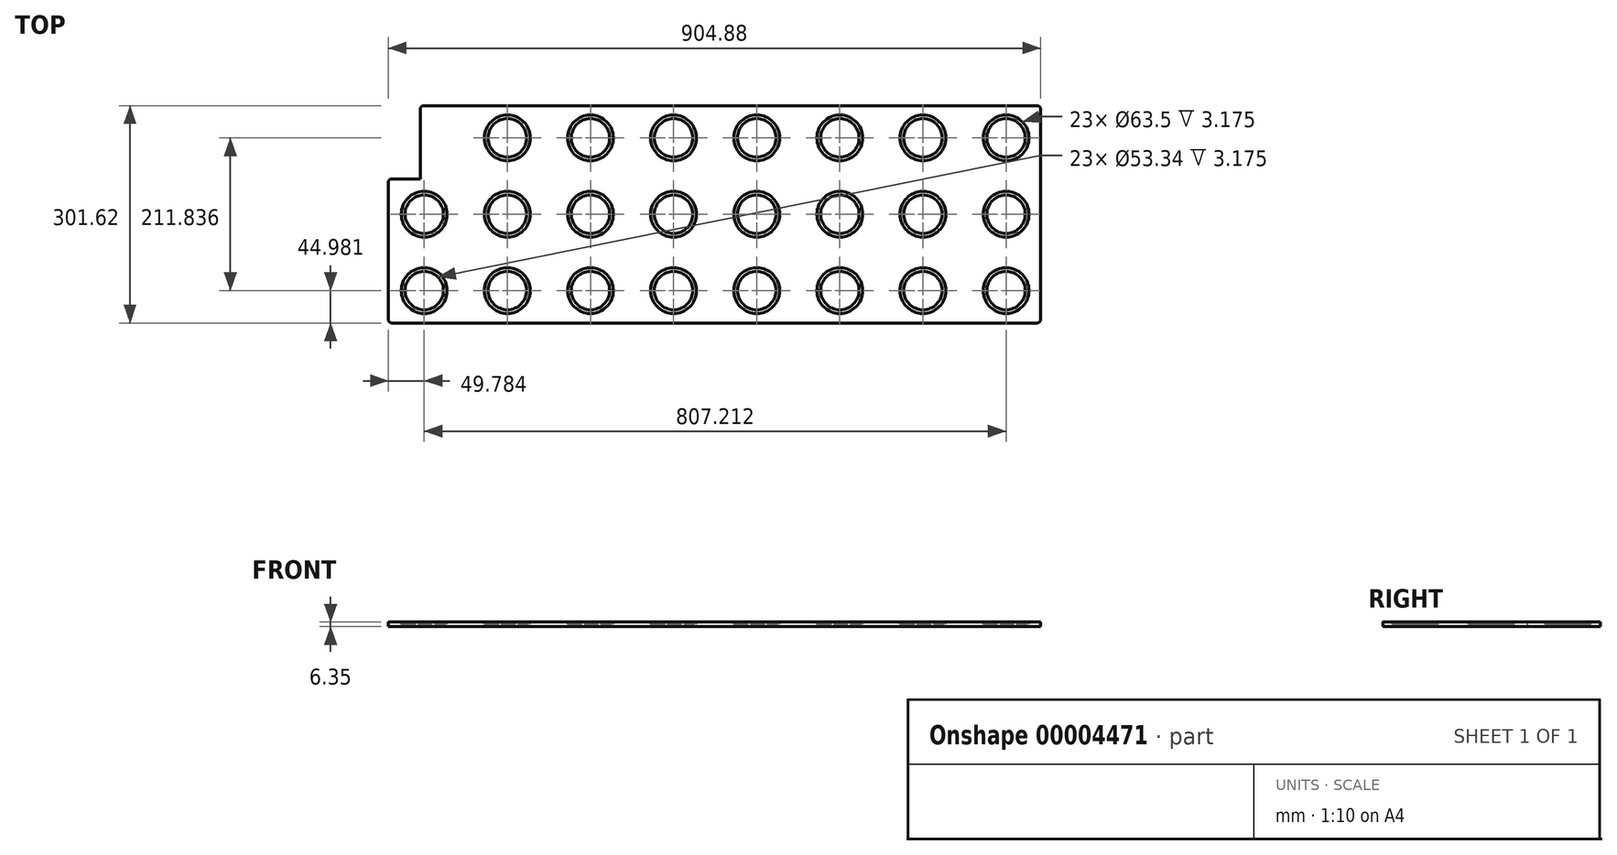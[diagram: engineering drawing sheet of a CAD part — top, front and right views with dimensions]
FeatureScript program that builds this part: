
annotation { "Feature Type Name" : "Feature", "Feature Type Description" : "" }
export const myFeature = defineFeature(function(context is Context, id is Id, definition is map)
    precondition{}
    {
        {
            var Q0;
            Q0=qCreatedBy(makeId("Top.planeOp"),FACE);
            var sketch = newSketch(context, id + "F0", { "sketchPlane" : qUnion([Q0])});
            skLineSegment(sketch, "E0", {"start": v(0, 0) * mm, "end": v(904.88, 0) * mm});
            skLineSegment(sketch, "E1", {"start": v(904.88, 0) * mm, "end": v(904.88, 301.62) * mm});
            skLineSegment(sketch, "E2", {"start": v(904.88, 301.63) * mm, "end": v(44.45, 301.63) * mm});
            skLineSegment(sketch, "E3", {"start": v(44.45, 301.62) * mm, "end": v(44.45, 200.02) * mm});
            skLineSegment(sketch, "E4", {"start": v(44.45, 200.02) * mm, "end": v(0, 200.02) * mm});
            skLineSegment(sketch, "E5", {"start": v(0, 200.02) * mm, "end": v(0, 0) * mm});
            skSolve(sketch);
        }
        {
            var Q0;
            Q0=qSketchRegion(id+"F0",true);
            extrude(context, id + "F1", {"entities" : qUnion([Q0]), "depth" : 6.35 * mm});
        }
        {
            var Q0;
            Q0=makeQuery(id+"F1.opExtrude","CAP_FACE",FACE,{"disambiguationData":[OSD([sQuery(id+"F0.wireOp",EDGE,"E0"),sQuery(id+"F0.wireOp",EDGE,"E1"),sQuery(id+"F0.wireOp",EDGE,"E2"),sQuery(id+"F0.wireOp",EDGE,"E3"),sQuery(id+"F0.wireOp",EDGE,"E4"),sQuery(id+"F0.wireOp",EDGE,"E5")])],"isStart":false});
            var sketch = newSketch(context, id + "F2", { "sketchPlane" : qUnion([Q0])});
            skCircle(sketch, "E6", {"center": v(49.78, 44.98) * mm, "radius": 31.75 * mm});
            skCircle(sketch, "E7.0.1.0", {"center": v(49.78, 150.9) * mm, "radius": 31.75 * mm});
            skCircle(sketch, "E7.1.0.0", {"center": v(165.1, 44.98) * mm, "radius": 31.75 * mm});
            skCircle(sketch, "E7.1.1.0", {"center": v(165.1, 150.9) * mm, "radius": 31.75 * mm});
            skCircle(sketch, "E7.1.2.0", {"center": v(165.1, 256.82) * mm, "radius": 31.75 * mm});
            skCircle(sketch, "E7.2.0.0", {"center": v(280.42, 44.98) * mm, "radius": 31.75 * mm});
            skCircle(sketch, "E7.2.1.0", {"center": v(280.42, 150.9) * mm, "radius": 31.75 * mm});
            skCircle(sketch, "E7.2.2.0", {"center": v(280.42, 256.82) * mm, "radius": 31.75 * mm});
            skCircle(sketch, "E7.3.0.0", {"center": v(395.73, 44.98) * mm, "radius": 31.75 * mm});
            skCircle(sketch, "E7.3.1.0", {"center": v(395.73, 150.9) * mm, "radius": 31.75 * mm});
            skCircle(sketch, "E7.3.2.0", {"center": v(395.73, 256.82) * mm, "radius": 31.75 * mm});
            skCircle(sketch, "E7.4.0.0", {"center": v(511.05, 44.98) * mm, "radius": 31.75 * mm});
            skCircle(sketch, "E7.4.1.0", {"center": v(511.05, 150.9) * mm, "radius": 31.75 * mm});
            skCircle(sketch, "E7.4.2.0", {"center": v(511.05, 256.82) * mm, "radius": 31.75 * mm});
            skCircle(sketch, "E7.5.0.0", {"center": v(626.36, 44.98) * mm, "radius": 31.75 * mm});
            skCircle(sketch, "E7.5.1.0", {"center": v(626.36, 150.9) * mm, "radius": 31.75 * mm});
            skCircle(sketch, "E7.5.2.0", {"center": v(626.36, 256.82) * mm, "radius": 31.75 * mm});
            skCircle(sketch, "E7.6.0.0", {"center": v(741.68, 44.98) * mm, "radius": 31.75 * mm});
            skCircle(sketch, "E7.6.1.0", {"center": v(741.68, 150.9) * mm, "radius": 31.75 * mm});
            skCircle(sketch, "E7.6.2.0", {"center": v(741.68, 256.82) * mm, "radius": 31.75 * mm});
            skCircle(sketch, "E7.7.0.0", {"center": v(857, 44.98) * mm, "radius": 31.75 * mm});
            skCircle(sketch, "E7.7.1.0", {"center": v(857, 150.9) * mm, "radius": 31.75 * mm});
            skCircle(sketch, "E7.7.2.0", {"center": v(857, 256.82) * mm, "radius": 31.75 * mm});
            skLineSegment(sketch, "E7.direction1", {"start": v(49.78, 44.98) * mm, "end": v(165.1, 44.98) * mm, "construction": true});
            skLineSegment(sketch, "E7.direction2", {"start": v(49.78, 44.98) * mm, "end": v(49.78, 150.9) * mm, "construction": true});
            skSolve(sketch);
        }
        {
            var Q0;
            Q0=qSketchRegion(id+"F2",true);
            extrude(context, id + "F3", {"entities" : qUnion([Q0]), "operationType" : NewBodyOperationType.REMOVE, "endBound" : BoundingType.THROUGH_ALL, "oppositeDirection" : true, "depth" : 25.4 * mm});
        }
        {
            var Q0;
            Q0=makeQuery(id+"F1.opExtrude","CAP_FACE",FACE,{"disambiguationData":[OSD([sQuery(id+"F0.wireOp",EDGE,"E0"),sQuery(id+"F0.wireOp",EDGE,"E1"),sQuery(id+"F0.wireOp",EDGE,"E2"),sQuery(id+"F0.wireOp",EDGE,"E3"),sQuery(id+"F0.wireOp",EDGE,"E4"),sQuery(id+"F0.wireOp",EDGE,"E5")])],"isStart":true});
            var sketch = newSketch(context, id + "F4", { "sketchPlane" : qUnion([Q0])});
            skCircle(sketch, "E8", {"center": v(49.78, -44.98) * mm, "radius": 26.67 * mm});
            skCircle(sketch, "E9.0.1.0", {"center": v(49.78, -150.9) * mm, "radius": 26.67 * mm});
            skCircle(sketch, "E9.1.0.0", {"center": v(165.1, -44.98) * mm, "radius": 26.67 * mm});
            skCircle(sketch, "E9.1.1.0", {"center": v(165.1, -150.9) * mm, "radius": 26.67 * mm});
            skCircle(sketch, "E9.1.2.0", {"center": v(165.1, -256.82) * mm, "radius": 26.67 * mm});
            skCircle(sketch, "E9.2.0.0", {"center": v(280.42, -44.98) * mm, "radius": 26.67 * mm});
            skCircle(sketch, "E9.2.1.0", {"center": v(280.42, -150.9) * mm, "radius": 26.67 * mm});
            skCircle(sketch, "E9.2.2.0", {"center": v(280.42, -256.82) * mm, "radius": 26.67 * mm});
            skCircle(sketch, "E9.3.0.0", {"center": v(395.73, -44.98) * mm, "radius": 26.67 * mm});
            skCircle(sketch, "E9.3.1.0", {"center": v(395.73, -150.9) * mm, "radius": 26.67 * mm});
            skCircle(sketch, "E9.3.2.0", {"center": v(395.73, -256.82) * mm, "radius": 26.67 * mm});
            skCircle(sketch, "E9.4.0.0", {"center": v(511.05, -44.98) * mm, "radius": 26.67 * mm});
            skCircle(sketch, "E9.4.1.0", {"center": v(511.05, -150.9) * mm, "radius": 26.67 * mm});
            skCircle(sketch, "E9.4.2.0", {"center": v(511.05, -256.82) * mm, "radius": 26.67 * mm});
            skCircle(sketch, "E9.5.0.0", {"center": v(626.36, -44.98) * mm, "radius": 26.67 * mm});
            skCircle(sketch, "E9.5.1.0", {"center": v(626.36, -150.9) * mm, "radius": 26.67 * mm});
            skCircle(sketch, "E9.5.2.0", {"center": v(626.36, -256.82) * mm, "radius": 26.67 * mm});
            skCircle(sketch, "E9.6.0.0", {"center": v(741.68, -44.98) * mm, "radius": 26.67 * mm});
            skCircle(sketch, "E9.6.1.0", {"center": v(741.68, -150.9) * mm, "radius": 26.67 * mm});
            skCircle(sketch, "E9.6.2.0", {"center": v(741.68, -256.82) * mm, "radius": 26.67 * mm});
            skCircle(sketch, "E9.7.0.0", {"center": v(857, -44.98) * mm, "radius": 26.67 * mm});
            skCircle(sketch, "E9.7.1.0", {"center": v(857, -150.9) * mm, "radius": 26.67 * mm});
            skCircle(sketch, "E9.7.2.0", {"center": v(857, -256.82) * mm, "radius": 26.67 * mm});
            skLineSegment(sketch, "E9.direction1", {"start": v(49.78, -44.98) * mm, "end": v(165.1, -44.98) * mm, "construction": true});
            skLineSegment(sketch, "E9.direction2", {"start": v(49.78, -44.98) * mm, "end": v(49.78, -150.9) * mm, "construction": true});
            skLineSegment(sketch, "E10", {"start": v(0, -200.02) * mm, "end": v(0, 0) * mm});
            skLineSegment(sketch, "E11", {"start": v(0, 0) * mm, "end": v(904.88, 0) * mm});
            skLineSegment(sketch, "E12", {"start": v(904.88, 0) * mm, "end": v(904.88, -301.63) * mm});
            skLineSegment(sketch, "E13", {"start": v(904.88, -301.63) * mm, "end": v(44.45, -301.62) * mm});
            skLineSegment(sketch, "E14", {"start": v(44.45, -301.62) * mm, "end": v(44.45, -200.02) * mm});
            skLineSegment(sketch, "E15", {"start": v(44.45, -200.02) * mm, "end": v(0, -200.02) * mm});
            skSolve(sketch);
        }
        {
            var Q0;
            Q0=qSketchRegion(id+"F4",true);
            extrude(context, id + "F5", {"entities" : qUnion([Q0]), "operationType" : NewBodyOperationType.ADD, "oppositeDirection" : true, "depth" : 3.17 * mm});
        }
        {
            var Q0;
            Q0=makeQuery(id+"F1.opExtrude","SWEPT_EDGE",EDGE,{"disambiguationData":[OSD([sQuery(id+"F0.wireOp",EDGE,"E4"),sQuery(id+"F0.wireOp",EDGE,"E5")])]});
            var Q1;
            Q1=makeQuery(id+"F1.opExtrude","SWEPT_EDGE",EDGE,{"disambiguationData":[OSD([sQuery(id+"F0.wireOp",EDGE,"E2"),sQuery(id+"F0.wireOp",EDGE,"E3")])]});
            var Q2;
            Q2=makeQuery(id+"F1.opExtrude","SWEPT_EDGE",EDGE,{"disambiguationData":[OSD([sQuery(id+"F0.wireOp",EDGE,"E0"),sQuery(id+"F0.wireOp",EDGE,"E5")])]});
            var Q3;
            Q3=makeQuery(id+"F1.opExtrude","SWEPT_EDGE",EDGE,{"disambiguationData":[OSD([sQuery(id+"F0.wireOp",EDGE,"E0"),sQuery(id+"F0.wireOp",EDGE,"E1")])]});
            var Q4;
            Q4=makeQuery(id+"F1.opExtrude","SWEPT_EDGE",EDGE,{"disambiguationData":[OSD([sQuery(id+"F0.wireOp",EDGE,"E1"),sQuery(id+"F0.wireOp",EDGE,"E2")])]});
            fillet(context, id + "F6", {"entities" : qUnion([Q0, Q1, Q2, Q3, Q4]), "radius" : 5.08 * mm, "tangentPropagation" : true, "allowEdgeOverflow" : false});
        }
    });
